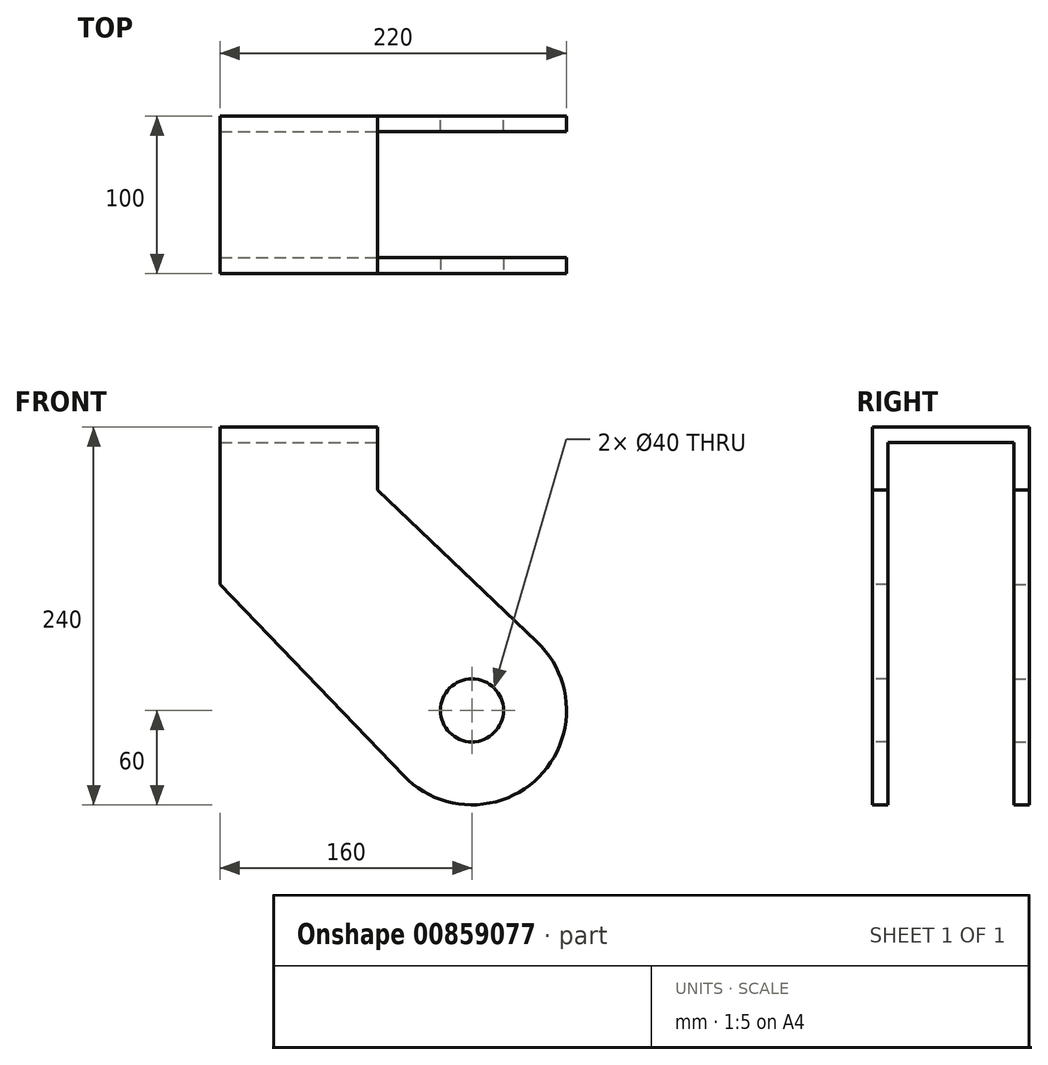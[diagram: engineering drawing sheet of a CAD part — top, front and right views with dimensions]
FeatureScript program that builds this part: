
annotation { "Feature Type Name" : "Feature", "Feature Type Description" : "" }
export const myFeature = defineFeature(function(context is Context, id is Id, definition is map)
    precondition{}
    {
        {
            var Q0;
            Q0=qCreatedBy(makeId("Front.planeOp"),FACE);
            var sketch = newSketch(context, id + "F0", { "sketchPlane" : qUnion([Q0])});
            skLineSegment(sketch, "E0", {"start": v(0, 0) * mm, "end": v(100, 0) * mm});
            skLineSegment(sketch, "E1", {"start": v(100, 0) * mm, "end": v(100, -40) * mm});
            skLineSegment(sketch, "E2", {"start": v(0, 0) * mm, "end": v(0, -100) * mm});
            skLineSegment(sketch, "E3", {"start": v(160, -129.68) * mm, "end": v(160, -304.68) * mm, "construction": true});
            skLineSegment(sketch, "E4", {"start": v(136.46, -180) * mm, "end": v(320.7, -180) * mm, "construction": true});
            skArc(sketch, "E5", {"start": v(116.72, -221.56) * mm, "mid": v(202.51, -222.34) * mm, "end": v(201.38, -136.55) * mm});
            skLineSegment(sketch, "E6", {"start": v(100, -40) * mm, "end": v(201.38, -136.55) * mm});
            skLineSegment(sketch, "E7", {"start": v(0, -100) * mm, "end": v(116.72, -221.56) * mm});
            skCircle(sketch, "E8", {"center": v(160, -180) * mm, "radius": 20 * mm});
            skSolve(sketch);
        }
        {
            var Q0;
            Q0=makeQuery(id+"F0.imprint","IMPRINT",FACE,{"disambiguationData":[TD([[makeQuery(id+"F0.imprint","IMPRINT",EDGE,{"derivedFrom":sQuery(id+"F0.wireOp",EDGE,"E0")}),-1.0]])]});
            extrude(context, id + "F1", {"entities" : qUnion([Q0]), "oppositeDirection" : true, "depth" : 10 * mm, "offsetDistance" : 25 * mm});
        }
        {
            var Q0;
            Q0=qCreatedBy(makeId("Front.planeOp"),FACE);
            cPlane(context, id + "F2", {"entities" : qUnion([Q0]), "cplaneType" : CPlaneType.OFFSET, "offset" : 50 * mm, "oppositeDirection" : true, "width" : 150 * mm, "height" : 150 * mm});
        }
        {
            var Q0;
            Q0=makeQuery(id+"F1.opExtrude","SWEPT_BODY",BODY,{"disambiguationData":[OSD([sQuery(id+"F0.wireOp",EDGE,"E0"),sQuery(id+"F0.wireOp",EDGE,"E1"),sQuery(id+"F0.wireOp",EDGE,"E2"),sQuery(id+"F0.wireOp",EDGE,"E5"),sQuery(id+"F0.wireOp",EDGE,"E6"),sQuery(id+"F0.wireOp",EDGE,"E7"),sQuery(id+"F0.wireOp",EDGE,"E8")])]});
            var Q1;
            Q1=qCreatedBy(id+"F2.planeOp",FACE);
            mirror(context, id + "F3", {"entities" : qUnion([Q0]), "mirrorPlane" : qUnion([Q1])});
        }
        {
            var Q0;
            Q0=makeQuery(id+"F3.opPattern","COPY",FACE,{"derivedFrom":makeQuery(id+"F1.opExtrude","CAP_FACE",FACE,{"disambiguationData":[OSD([sQuery(id+"F0.wireOp",EDGE,"E0"),sQuery(id+"F0.wireOp",EDGE,"E1"),sQuery(id+"F0.wireOp",EDGE,"E2"),sQuery(id+"F0.wireOp",EDGE,"E5"),sQuery(id+"F0.wireOp",EDGE,"E6"),sQuery(id+"F0.wireOp",EDGE,"E7"),sQuery(id+"F0.wireOp",EDGE,"E8")])],"isStart":false}),"instanceName":"1"});
            var sketch = newSketch(context, id + "F4", { "sketchPlane" : qUnion([Q0])});
            skLineSegment(sketch, "E9.0", {"start": v(0, 0) * mm, "end": v(100, 0) * mm});
            skLineSegment(sketch, "E10.0", {"start": v(100, 0) * mm, "end": v(100, -10) * mm});
            skLineSegment(sketch, "E11.0", {"start": v(0, 0) * mm, "end": v(0, -10) * mm});
            skLineSegment(sketch, "E12", {"start": v(0, -10) * mm, "end": v(100, -10) * mm});
            skPoint(sketch, "E13.orphan", {"position": v(0, -100) * mm});
            skPoint(sketch, "E14.orphan", {"position": v(100, -40) * mm});
            skSolve(sketch);
        }
        {
            var Q0;
            Q0 = qSketchRegion(id + "F4", true);
            var Q1;
            Q1=makeQuery(id+"F1.opExtrude","CAP_FACE",FACE,{"disambiguationData":[OSD([sQuery(id+"F0.wireOp",EDGE,"E0"),sQuery(id+"F0.wireOp",EDGE,"E1"),sQuery(id+"F0.wireOp",EDGE,"E2"),sQuery(id+"F0.wireOp",EDGE,"E5"),sQuery(id+"F0.wireOp",EDGE,"E6"),sQuery(id+"F0.wireOp",EDGE,"E7"),sQuery(id+"F0.wireOp",EDGE,"E8")])],"isStart":false});
            extrude(context, id + "F5", {"entities" : qUnion([Q0]), "operationType" : NewBodyOperationType.ADD, "endBound" : BoundingType.UP_TO_SURFACE, "depth" : 25 * mm, "endBoundEntityFace" : qUnion([Q1]), "offsetDistance" : 25 * mm});
        }
    });
